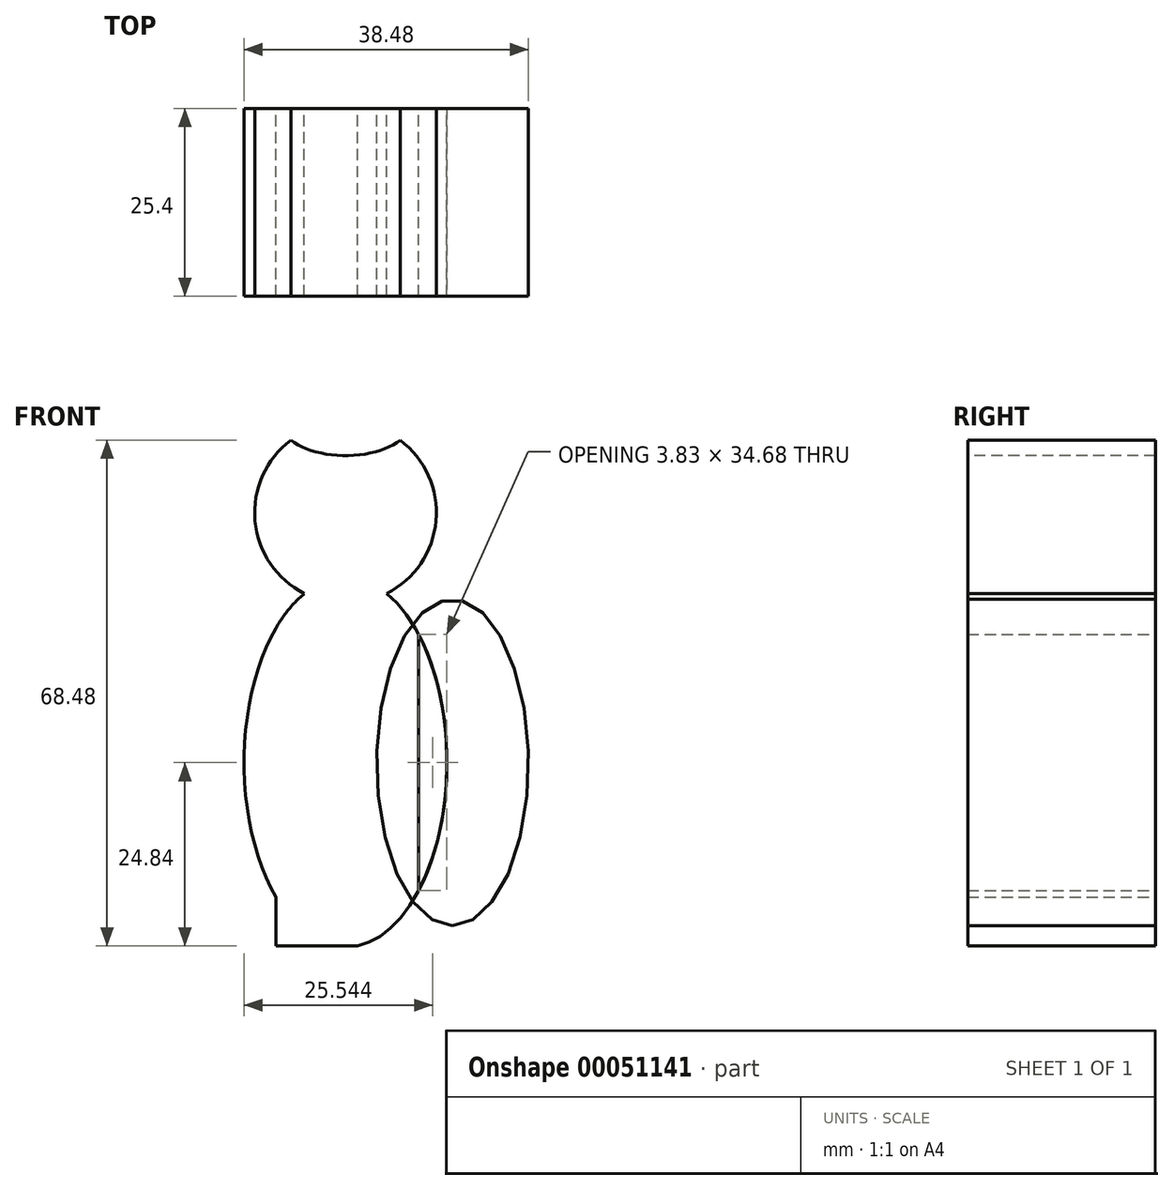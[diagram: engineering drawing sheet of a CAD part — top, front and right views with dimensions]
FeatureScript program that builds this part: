
annotation { "Feature Type Name" : "Feature", "Feature Type Description" : "" }
export const myFeature = defineFeature(function(context is Context, id is Id, definition is map)
    precondition{}
    {
        {
            var Q0;
            Q0=qCreatedBy(makeId("Front.planeOp"),FACE);
            var sketch = newSketch(context, id + "F0", { "sketchPlane" : qUnion([Q0])});
            skEllipse(sketch, "E0", {"center": v(0, 0) * mm, "majorRadius": 25.02 * mm, "minorRadius": 13.73 * mm, "majorAxis": v(0, -1)});
            skLineSegment(sketch, "E1.bottom", {"start": v(-9.43, 18.19) * mm, "end": v(9.9, 18.19) * mm});
            skLineSegment(sketch, "E1.top", {"start": v(-9.43, -24.84) * mm, "end": v(9.9, -24.84) * mm});
            skLineSegment(sketch, "E1.left", {"start": v(-9.43, 18.19) * mm, "end": v(-9.43, -24.84) * mm});
            skLineSegment(sketch, "E1.right", {"start": v(9.9, 18.19) * mm, "end": v(9.9, -24.84) * mm});
            skCircle(sketch, "E2", {"center": v(0, 33.82) * mm, "radius": 12.3 * mm});
            skPoint(sketch, "E2.centerSnap0", {"position": v(0, 25.02) * mm});
            skEllipse(sketch, "E3", {"center": v(0, 46.1) * mm, "majorRadius": 8.8 * mm, "minorRadius": 4.56 * mm, "majorAxis": v(-1, 0)});
            skSolve(sketch);
        }
        {
            var Q0;
            {var subQ2=sQuery(id+"F0.wireOp",EDGE,"E0");var subQ5=sQuery(id+"F0.wireOp",EDGE,"E1.right");var subQ10=makeQuery(id+"F0.imprint","INTERSECT",VERTEX,{"disambiguationData":[OD(0.0)],"derivedFrom":[subQ2,subQ5]});Q0=makeQuery(id+"F0.imprint","IMPRINT",FACE,{"disambiguationData":[TD([[makeQuery(id+"F0.imprint","IMPRINT",EDGE,{"disambiguationData":[TD([[subQ10,1.0]])],"derivedFrom":subQ2}),1.0]])]});}
            var sketch = newSketch(context, id + "F1", { "sketchPlane" : qUnion([Q0])});
            skEllipse(sketch, "E4", {"center": v(-13.75, 0) * mm, "majorRadius": 21.72 * mm, "minorRadius": 9.4 * mm, "majorAxis": v(0, -1)});
            skEllipse(sketch, "E5", {"center": v(14.48, 0) * mm, "majorRadius": 22.09 * mm, "minorRadius": 10.27 * mm, "majorAxis": v(0, -1)});
            skSolve(sketch);
        }
        {
            var Q0;
            {var subQ1=sQuery(id+"F0.wireOp",EDGE,"E1.left");var subQ2=sQuery(id+"F0.wireOp",EDGE,"E0");var subQ3=makeQuery(id+"F0.imprint","INTERSECT",VERTEX,{"derivedFrom":[subQ2,subQ1]});var subQ10=makeQuery(id+"F0.imprint","IMPRINT",EDGE,{"disambiguationData":[TD([[subQ3,1.0]])],"derivedFrom":subQ1});Q0=makeQuery(id+"F1.imprint","IMPRINT",FACE,{"disambiguationData":[TD([[makeQuery(id+"F1.imprint","IMPRINT",EDGE,{"derivedFrom":subQ10}),-1.0]])]});}
            var sketch = newSketch(context, id + "F2", { "sketchPlane" : qUnion([Q0])});
            skEllipse(sketch, "E6", {"center": v(-19.06, -12) * mm, "majorRadius": 6.97 * mm, "minorRadius": 2.96 * mm, "majorAxis": v(0, -1)});
            skEllipse(sketch, "E7", {"center": v(-21.26, 0) * mm, "majorRadius": 6.87 * mm, "minorRadius": 3.27 * mm, "majorAxis": v(0, -1)});
            skEllipse(sketch, "E8", {"center": v(24.93, 0) * mm, "majorRadius": 7.24 * mm, "minorRadius": 1.14 * mm, "majorAxis": v(0, -1)});
            skEllipse(sketch, "E9", {"center": v(21.08, -12) * mm, "majorRadius": 6.42 * mm, "minorRadius": 2.62 * mm, "majorAxis": v(0, -1)});
            skPoint(sketch, "E9.centerSnap0", {"position": v(-16.1, -12) * mm});
            skSolve(sketch);
        }
        {
            var Q0;
            {var subQ0=sQuery(id+"F0.wireOp",EDGE,"E2");var subQ1=sQuery(id+"F0.wireOp",EDGE,"E0");var subQ2=makeQuery(id+"F0.imprint","INTERSECT",VERTEX,{"disambiguationData":[OD(0.0)],"derivedFrom":[subQ1,subQ0]});Q0=makeQuery(id+"F0.imprint","IMPRINT",FACE,{"disambiguationData":[TD([[makeQuery(id+"F0.imprint","IMPRINT",EDGE,{"disambiguationData":[TD([[subQ2,-1.0]])],"derivedFrom":subQ1}),-1.0]])]});}
            var Q1;
            {var subQ0=sQuery(id+"F0.wireOp",EDGE,"E3");var subQ1=sQuery(id+"F0.wireOp",EDGE,"E2");var subQ2=makeQuery(id+"F0.imprint","INTERSECT",VERTEX,{"disambiguationData":[OD(0.0)],"derivedFrom":[subQ1,subQ0]});Q1=makeQuery(id+"F0.imprint","IMPRINT",FACE,{"disambiguationData":[TD([[makeQuery(id+"F0.imprint","IMPRINT",EDGE,{"disambiguationData":[TD([[subQ2,1.0]])],"derivedFrom":subQ1}),1.0]])]});}
            var Q2;
            {var subQ0=sQuery(id+"F0.wireOp",EDGE,"E3");var subQ1=sQuery(id+"F0.wireOp",EDGE,"E2");var subQ2=makeQuery(id+"F0.imprint","INTERSECT",VERTEX,{"disambiguationData":[OD(0.0)],"derivedFrom":[subQ1,subQ0]});Q2=makeQuery(id+"F0.imprint","IMPRINT",FACE,{"disambiguationData":[TD([[makeQuery(id+"F0.imprint","IMPRINT",EDGE,{"disambiguationData":[TD([[subQ2,1.0]])],"derivedFrom":subQ1}),-1.0]])]});}
            var Q3;
            {var subQ0=sQuery(id+"F0.wireOp",EDGE,"E2");var subQ1=sQuery(id+"F0.wireOp",EDGE,"E0");var subQ2=makeQuery(id+"F0.imprint","INTERSECT",VERTEX,{"disambiguationData":[OD(0.0)],"derivedFrom":[subQ1,subQ0]});Q3=makeQuery(id+"F0.imprint","IMPRINT",FACE,{"disambiguationData":[TD([[makeQuery(id+"F0.imprint","IMPRINT",EDGE,{"disambiguationData":[TD([[subQ2,-1.0]])],"derivedFrom":subQ1}),1.0]])]});}
            var Q4;
            {var subQ0=sQuery(id+"F0.wireOp",EDGE,"E1.bottom");var subQ1=sQuery(id+"F0.wireOp",EDGE,"E0");var subQ2=makeQuery(id+"F0.imprint","INTERSECT",VERTEX,{"derivedFrom":[subQ1,subQ0]});Q4=makeQuery(id+"F0.imprint","IMPRINT",FACE,{"disambiguationData":[TD([[makeQuery(id+"F0.imprint","IMPRINT",EDGE,{"disambiguationData":[TD([[subQ2,-1.0]])],"derivedFrom":subQ1}),1.0]])]});}
            var Q5;
            {var subQ2=sQuery(id+"F0.wireOp",EDGE,"E0");var subQ5=sQuery(id+"F0.wireOp",EDGE,"E1.right");var subQ10=makeQuery(id+"F0.imprint","INTERSECT",VERTEX,{"disambiguationData":[OD(0.0)],"derivedFrom":[subQ2,subQ5]});Q5=makeQuery(id+"F0.imprint","IMPRINT",FACE,{"disambiguationData":[TD([[makeQuery(id+"F0.imprint","IMPRINT",EDGE,{"disambiguationData":[TD([[subQ10,1.0]])],"derivedFrom":subQ2}),1.0]])]});}
            var Q6;
            {var subQ0=sQuery(id+"F0.wireOp",EDGE,"E1.left");var subQ1=sQuery(id+"F0.wireOp",EDGE,"E0");var subQ3=makeQuery(id+"F0.imprint","INTERSECT",VERTEX,{"derivedFrom":[subQ1,subQ0]});Q6=makeQuery(id+"F0.imprint","IMPRINT",FACE,{"disambiguationData":[TD([[makeQuery(id+"F0.imprint","IMPRINT",EDGE,{"disambiguationData":[TD([[subQ3,1.0]])],"derivedFrom":subQ1}),1.0]])]});}
            var Q7;
            {var subQ0=sQuery(id+"F0.wireOp",EDGE,"E1.right");var subQ1=sQuery(id+"F0.wireOp",EDGE,"E0");var subQ2=makeQuery(id+"F0.imprint","INTERSECT",VERTEX,{"disambiguationData":[OD(0.0)],"derivedFrom":[subQ1,subQ0]});Q7=makeQuery(id+"F0.imprint","IMPRINT",FACE,{"disambiguationData":[TD([[makeQuery(id+"F0.imprint","IMPRINT",EDGE,{"disambiguationData":[TD([[subQ2,-1.0]])],"derivedFrom":subQ1}),1.0]])]});}
            var Q8;
            {var subQ0=sQuery(id+"F0.wireOp",EDGE,"E1.right");var subQ1=sQuery(id+"F0.wireOp",EDGE,"E0");var subQ3=makeQuery(id+"F0.imprint","INTERSECT",VERTEX,{"disambiguationData":[OD(1.0)],"derivedFrom":[subQ1,subQ0]});var subQ10=makeQuery(id+"F0.imprint","IMPRINT",EDGE,{"disambiguationData":[TD([[subQ3,-1.0]])],"derivedFrom":subQ1});Q8=makeQuery(id+"F1.imprint","IMPRINT",FACE,{"disambiguationData":[TD([[makeQuery(id+"F1.imprint","IMPRINT",EDGE,{"derivedFrom":subQ10}),-1.0]])]});}
            var Q9;
            {var subQ0=sQuery(id+"F0.wireOp",EDGE,"E1.left");var subQ1=sQuery(id+"F0.wireOp",EDGE,"E0");var subQ2=makeQuery(id+"F0.imprint","INTERSECT",VERTEX,{"derivedFrom":[subQ1,subQ0]});Q9=makeQuery(id+"F0.imprint","IMPRINT",FACE,{"disambiguationData":[TD([[makeQuery(id+"F0.imprint","IMPRINT",EDGE,{"disambiguationData":[TD([[subQ2,-1.0]])],"derivedFrom":subQ1}),-1.0]])]});}
            var Q10;
            {var subQ0=sQuery(id+"F0.wireOp",EDGE,"E1.right");var subQ1=sQuery(id+"F0.wireOp",EDGE,"E0");var subQ2=makeQuery(id+"F0.imprint","INTERSECT",VERTEX,{"disambiguationData":[OD(0.0)],"derivedFrom":[subQ1,subQ0]});Q10=makeQuery(id+"F0.imprint","IMPRINT",FACE,{"disambiguationData":[TD([[makeQuery(id+"F0.imprint","IMPRINT",EDGE,{"disambiguationData":[TD([[subQ2,1.0]])],"derivedFrom":subQ1}),-1.0]])]});}
            var Q11;
            {var subQ1=sQuery(id+"F0.wireOp",EDGE,"E1.left");var subQ2=sQuery(id+"F0.wireOp",EDGE,"E0");var subQ3=makeQuery(id+"F0.imprint","INTERSECT",VERTEX,{"derivedFrom":[subQ2,subQ1]});var subQ10=makeQuery(id+"F0.imprint","IMPRINT",EDGE,{"disambiguationData":[TD([[subQ3,1.0]])],"derivedFrom":subQ1});Q11=makeQuery(id+"F1.imprint","IMPRINT",FACE,{"disambiguationData":[TD([[makeQuery(id+"F1.imprint","IMPRINT",EDGE,{"derivedFrom":subQ10}),-1.0]])]});}
            var Q12;
            {var subQ0=sQuery(id+"F2.wireOp",EDGE,"E7");var subQ1=sQuery(id+"F1.wireOp",EDGE,"E4");var subQ2=sQuery(id+"F0.wireOp",EDGE,"E1.left");var subQ3=sQuery(id+"F0.wireOp",EDGE,"E0");var subQ5=makeQuery(id+"F1.imprint","IMPRINT",EDGE,{"disambiguationData":[TD([[makeQuery(id+"F1.imprint","INTERSECT",VERTEX,{"derivedFrom":[makeQuery(id+"F0.imprint","IMPRINT",EDGE,{"disambiguationData":[TD([[makeQuery(id+"F0.imprint","INTERSECT",VERTEX,{"derivedFrom":[subQ3,subQ2]}),-1.0]])],"derivedFrom":subQ3}),subQ1]}),1.0]])],"derivedFrom":subQ1});var subQ6=makeQuery(id+"F2.imprint","INTERSECT",VERTEX,{"disambiguationData":[OD(0.0)],"derivedFrom":[subQ5,subQ0]});Q12=makeQuery(id+"F2.imprint","IMPRINT",FACE,{"disambiguationData":[TD([[makeQuery(id+"F2.imprint","IMPRINT",EDGE,{"disambiguationData":[TD([[subQ6,-1.0]])],"derivedFrom":subQ0}),1.0]])]});}
            var Q13;
            {var subQ0=sQuery(id+"F2.wireOp",EDGE,"E6");var subQ1=sQuery(id+"F1.wireOp",EDGE,"E4");var subQ2=sQuery(id+"F0.wireOp",EDGE,"E1.left");var subQ3=sQuery(id+"F0.wireOp",EDGE,"E0");var subQ5=makeQuery(id+"F1.imprint","IMPRINT",EDGE,{"disambiguationData":[TD([[makeQuery(id+"F1.imprint","INTERSECT",VERTEX,{"derivedFrom":[makeQuery(id+"F0.imprint","IMPRINT",EDGE,{"disambiguationData":[TD([[makeQuery(id+"F0.imprint","INTERSECT",VERTEX,{"derivedFrom":[subQ3,subQ2]}),-1.0]])],"derivedFrom":subQ3}),subQ1]}),1.0]])],"derivedFrom":subQ1});var subQ6=makeQuery(id+"F2.imprint","INTERSECT",VERTEX,{"disambiguationData":[OD(0.0)],"derivedFrom":[subQ5,subQ0]});Q13=makeQuery(id+"F2.imprint","IMPRINT",FACE,{"disambiguationData":[TD([[makeQuery(id+"F2.imprint","IMPRINT",EDGE,{"disambiguationData":[TD([[subQ6,1.0]])],"derivedFrom":subQ0}),1.0]])]});}
            var Q14;
            Q14=makeQuery(id+"F2.imprint","IMPRINT",FACE,{"disambiguationData":[TD([[makeQuery(id+"F2.imprint","IMPRINT",EDGE,{"derivedFrom":sQuery(id+"F2.wireOp",EDGE,"E9")}),1.0]])]});
            var Q15;
            Q15=makeQuery(id+"F2.imprint","IMPRINT",FACE,{"disambiguationData":[TD([[makeQuery(id+"F2.imprint","IMPRINT",EDGE,{"derivedFrom":sQuery(id+"F2.wireOp",EDGE,"E8")}),1.0]])]});
            extrude(context, id + "F3", {"entities" : qUnion([Q0, Q1, Q2, Q3, Q4, Q5, Q6, Q7, Q8, Q9, Q10, Q11, Q12, Q13, Q14, Q15]), "depth" : 25.4 * mm});
        }
    });
